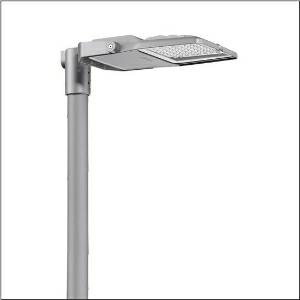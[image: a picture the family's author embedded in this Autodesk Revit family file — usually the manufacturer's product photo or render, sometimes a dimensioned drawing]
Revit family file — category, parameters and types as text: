
# Revit family: floodlight_fl_21_iq_mini___pl61_5xa7771b4c3a_e6c4
name_source: partatom
category: Lighting Fixtures
units: mm (PartAtom-declared; Revit-internal decimal feet)

## family parameters
Cut with Voids When Loaded = No
Host = Face
Light Source = No
Part Type = Normal
Room Calculation Point = No
Round Connector Dimension = Use Diameter
Shared = No

## types (1)
- --- (1 x LED, 6370 lm, 45.5 W, 4000K)
    Apparent Load = 46 VA
    CIE Flux Codes = 33 65 98 100 100
    Color Rendering = 70
    Color Temperature = 4000K
    Default Elevation = 1800 mm
    Description = Floodlight FL 21 iQ mini, floodlight, primary light control with lens, of PMMA, primary optical cover: protective disc, of toughened safety glass, transparent, light distribution: PL61, light emission: direct distribution, installation type: surface-mounted, lamps: LED, High Power LED, rated values: 6.370lm | 45,5W | 140lm/W (begin service life); end service life: 6.370lm | 48W; at 50% lumin. flux: 3.185lm | 21,5W | 148,1lm/W, colour temperature: 4000K, colour rendering: CRI > 70, light colour: 740, light setting 1 begin service life: 100% | 6.370lm | 45,5W | 140lm/W | 4.000K, light setting 1 end service life: 48W, further light settings possible, control: Auto-Match, Temp-Guard, Lumen-Switch, Night-Set, Smart-Wire, Light-Fading, Desk-Remote (wireless, voltage-free reading and setting of iQ features in the workshop via application-optimized NFC function/RFID function), optimised constant luminous flux control (CLO 2.0), pre-setting: linear dimming characteristic, with terminal, 6-pole, mains connection: 220..240V, AC, 50/60Hz, luminaire housing, of diecast aluminium, powder-coated, SITECO metallic grey (DB 702S), corrosivity category C5 mid according to DIN EN ISO 12944suitable for swimming poolschlorine-resistant, sealing non-destructively replaceable, please order mast flange separately, mast bracket, of steel, galvanised, powder-coated, SITECO metallic grey (DB 702S), protection rating (complete): IP66, insulation class (complete): insulation class II (safety insulation), certification: CE, ENEC, VDE, protection symbol: D, impact resistance: IK08, permissible operating ambient temperature: -40..+40°C, permissible operating ambient temperature for outdoor applications: -40..+50°C, standard: DIN EN 12944, LABS conformity tested according to VDMA 24364:2018-05, packaging unit: 1 piece

Light Distribution: PL61
    Height = 70 mm
    Lamp = 1 x LED
    Lamp Light Flux = 6370 lm
    Lamp Power = 45.5 W
    Lamp count = 1
    Length = 485 mm
    Luminous efficacy = 140 lm/W
    Manufacturer = Siteco
    ModVariant = No
    Model = 5XA7771B4C3A
    Number of Poles = 1
    OnlyDefault = Yes
    Power Factor = 1
    Product Name = Floodlight FL 21 iQ mini | PL61
    Product group = floodlight | pylon annexe
    ProductGroupID = 6201
    Protection Class = Protection class II
    Protection Degree = IP 66
    RLX_Detail_Level = 1
    RLX_Emergency_Light_Flux = 0 lm
    RLX_Emergency_Type = 0
    RLX_Emergency_Type_DB = No
    RlxData = <blob elided: 101585 chars, md5=3dca1c92>
    Socket = socket
    Standby Power = 0 W
    System Light Flux = 6370 lm
    System Power = 46 W
    Type Comments = factory setting: luminous flux: 100 % | dim-lin: 254 | 463 mA
    Type Image = l_1007125.jpg
    URL = http://relux.com
    VarID = @adj_173213
    Voltage = 0 V
    Weight = 0.00 kg
    Width = 337 mm

## geometry (parser evidence)
native form markers: Blend x4, Sweep x14
no freeform markers — native parametric forms only
